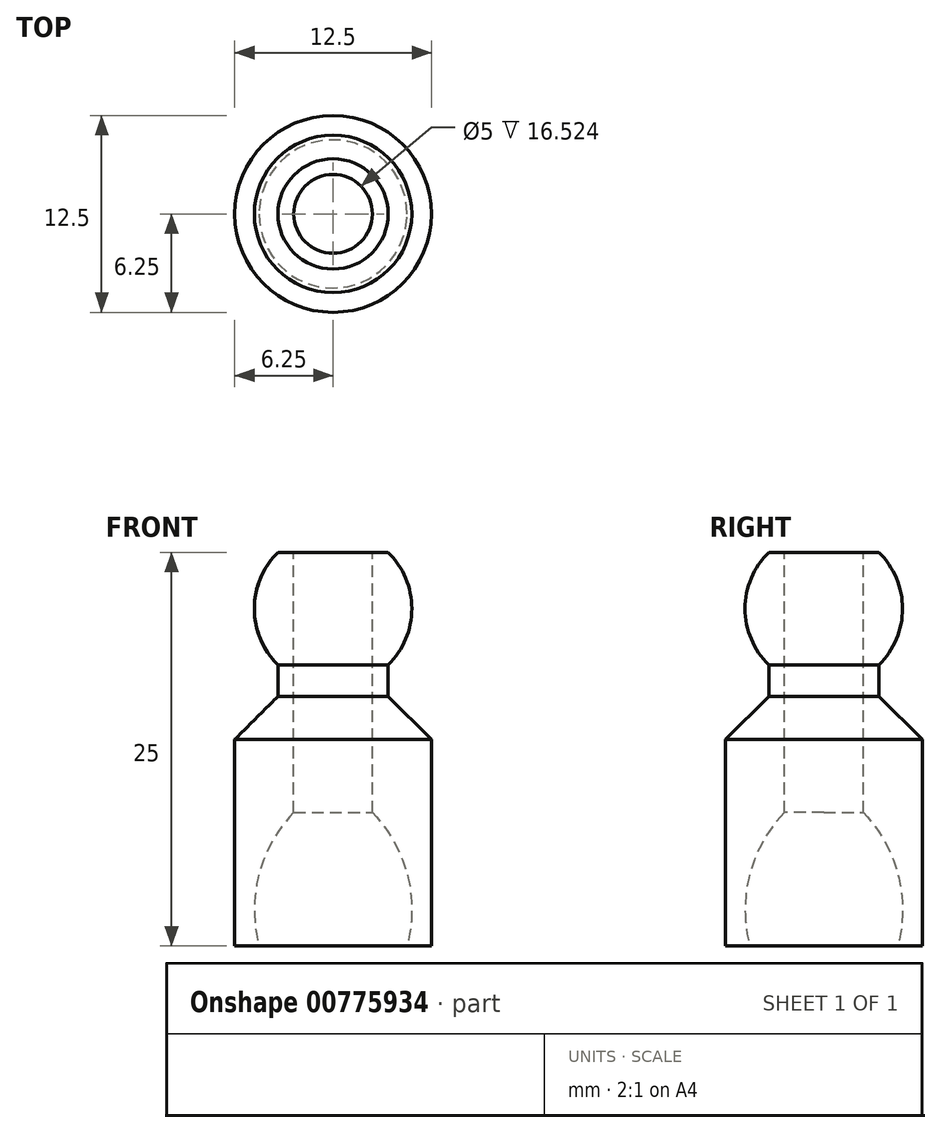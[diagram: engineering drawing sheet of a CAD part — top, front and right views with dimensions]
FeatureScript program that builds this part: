
annotation { "Feature Type Name" : "Feature", "Feature Type Description" : "" }
export const myFeature = defineFeature(function(context is Context, id is Id, definition is map)
    precondition{}
    {
        {
            var Q0;
            Q0=qCreatedBy(makeId("Front.planeOp"),FACE);
            var sketch = newSketch(context, id + "F0", { "sketchPlane" : qUnion([Q0])});
            skLineSegment(sketch, "E0", {"start": v(-6.25, 0) * mm, "end": v(-6.25, 13.1) * mm});
            skLineSegment(sketch, "E1", {"start": v(-6.25, 13.1) * mm, "end": v(-3.5, 15.86) * mm});
            skLineSegment(sketch, "E2", {"start": v(-3.5, 15.86) * mm, "end": v(-3.5, 17.86) * mm});
            skLineSegment(sketch, "E3", {"start": v(0, 0) * mm, "end": v(0, 25) * mm});
            skLineSegment(sketch, "E4", {"start": v(-3.5, 25) * mm, "end": v(0, 25) * mm});
            skArc(sketch, "E5", {"start": v(-3.5, 25) * mm, "mid": v(-5, 21.43) * mm, "end": v(-3.5, 17.86) * mm});
            skLineSegment(sketch, "E6", {"start": v(-6.25, 0) * mm, "end": v(0, 0) * mm});
            skSolve(sketch);
        }
        {
            var Q0;
            Q0=makeQuery(id+"F0.imprint","IMPRINT",FACE,{"disambiguationData":[TD([[makeQuery(id+"F0.imprint","IMPRINT",EDGE,{"derivedFrom":sQuery(id+"F0.wireOp",EDGE,"E0")}),-1.0]])]});
            var Q1;
            Q1=sQuery(id+"F0.wireOp",EDGE,"E3");
            revolve(context, id + "F1", {"surfaceOperationType" : NewSurfaceOperationType.NEW, "entities" : qUnion([Q0]), "axis" : qUnion([Q1]), "revolveType" : RevolveType.FULL});
        }
        {
            var Q0;
            Q0=qCreatedBy(makeId("Front.planeOp"),FACE);
            var sketch = newSketch(context, id + "F2", { "sketchPlane" : qUnion([Q0])});
            skLineSegment(sketch, "E7", {"start": v(0, -2.7) * mm, "end": v(0, 7.3) * mm, "construction": true});
            skArc(sketch, "E8", {"start": v(0, 7.3) * mm, "mid": v(-5, 2.3) * mm, "end": v(0, -2.7) * mm});
            skLineSegment(sketch, "E9", {"start": v(0, 7.3) * mm, "end": v(0, 7.3) * mm});
            skLineSegment(sketch, "E10", {"start": v(0, 7.3) * mm, "end": v(0, 0) * mm});
            skArc(sketch, "E11", {"start": v(0, 10.3) * mm, "mid": v(-5, 2.3) * mm, "end": v(0, -5.7) * mm});
            skLineSegment(sketch, "E12", {"start": v(0, 10.3) * mm, "end": v(0, 7.3) * mm});
            skLineSegment(sketch, "E13", {"start": v(0, 0) * mm, "end": v(-4.7, 0) * mm});
            skSolve(sketch);
        }
        {
            var Q0;
            Q0 = qSketchRegion(id + "F2", true);
            var Q1;
            Q1=sQuery(id+"F2.wireOp",EDGE,"E7");
            revolve(context, id + "F3", {"operationType" : NewBodyOperationType.REMOVE, "surfaceOperationType" : NewSurfaceOperationType.NEW, "entities" : qUnion([Q0]), "axis" : qUnion([Q1]), "revolveType" : RevolveType.FULL, "oppositeDirection" : true});
        }
        {
            var Q0;
            Q0=makeQuery(id+"F1.opRevolve","SWEPT_FACE",FACE,{"disambiguationData":[OSD([sQuery(id+"F0.wireOp",EDGE,"E4")])]});
            var sketch = newSketch(context, id + "F4", { "sketchPlane" : qUnion([Q0])});
            skCircle(sketch, "E14", {"center": v(0, 0) * mm, "radius": 2.5 * mm});
            skSolve(sketch);
        }
        {
            var Q0;
            Q0 = qSketchRegion(id + "F4", true);
            extrude(context, id + "F5", {"entities" : qUnion([Q0]), "operationType" : NewBodyOperationType.REMOVE, "endBound" : BoundingType.THROUGH_ALL, "oppositeDirection" : true, "depth" : 25 * mm, "offsetDistance" : 25 * mm});
        }
    });
